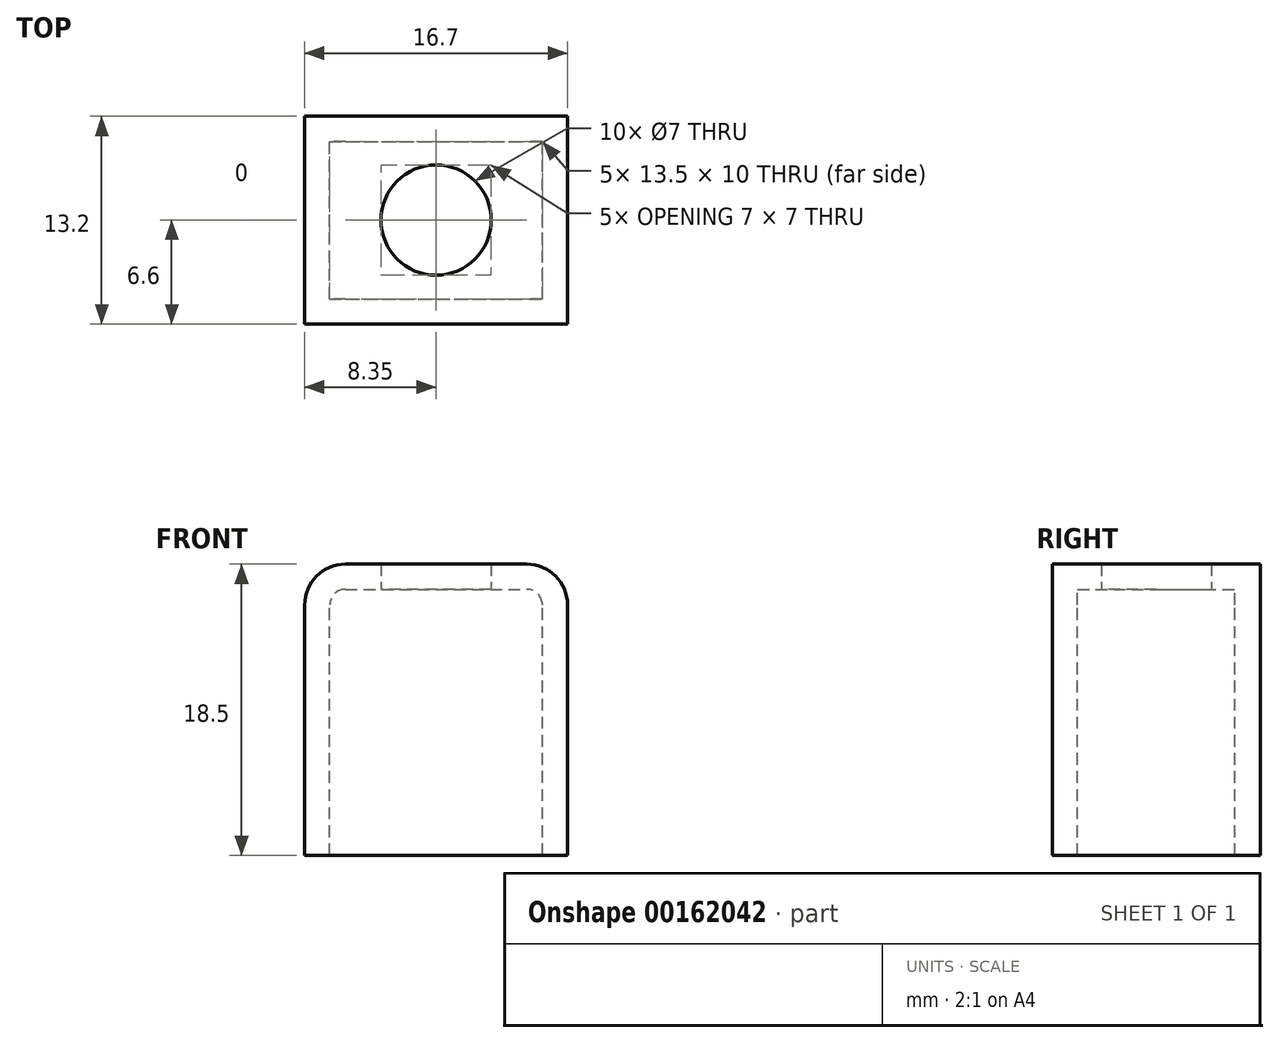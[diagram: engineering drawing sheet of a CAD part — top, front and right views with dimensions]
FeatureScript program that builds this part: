
annotation { "Feature Type Name" : "Feature", "Feature Type Description" : "" }
export const myFeature = defineFeature(function(context is Context, id is Id, definition is map)
    precondition{}
    {
        {
            var Q0;
            Q0=qCreatedBy(makeId("Front.planeOp"),FACE);
            var sketch = newSketch(context, id + "F0", { "sketchPlane" : qUnion([Q0])});
            skLineSegment(sketch, "E0.bottom", {"start": v(-8.35, 0) * mm, "end": v(8.35, 0) * mm});
            skLineSegment(sketch, "E0.top", {"start": v(-5.76, 18.5) * mm, "end": v(5.76, 18.5) * mm});
            skLineSegment(sketch, "E0.left", {"start": v(-8.35, 0) * mm, "end": v(-8.35, 15.9) * mm});
            skLineSegment(sketch, "E0.right", {"start": v(8.35, 0) * mm, "end": v(8.35, 15.9) * mm});
            skPoint(sketch, "E1.visualSharp", {"position": v(-8.35, 18.5) * mm});
            skArc(sketch, "E1.filletArc", {"start": v(-5.76, 18.5) * mm, "mid": v(-7.59, 17.74) * mm, "end": v(-8.35, 15.9) * mm});
            skPoint(sketch, "E2.visualSharp", {"position": v(8.35, 18.5) * mm});
            skArc(sketch, "E2.filletArc", {"start": v(8.35, 15.9) * mm, "mid": v(7.59, 17.74) * mm, "end": v(5.76, 18.5) * mm});
            skSolve(sketch);
        }
        {
            var Q0;
            Q0=qSketchRegion(id+"F0",true);
            extrude(context, id + "F1", {"entities" : qUnion([Q0]), "depth" : ((2 * 1.6) + 10) * mm});
        }
        {
            var Q0;
            Q0=makeQuery(id+"F1.opExtrude","SWEPT_FACE",FACE,{"disambiguationData":[OSD([sQuery(id+"F0.wireOp",EDGE,"E0.bottom")])]});
            shell(context, id + "F2", {"entities" : qUnion([Q0]), "thickness" : 1.6 * mm});
        }
        {
            var Q0;
            Q0=makeQuery(id+"F1.opExtrude","SWEPT_FACE",FACE,{"disambiguationData":[OSD([sQuery(id+"F0.wireOp",EDGE,"E0.top")])]});
            var sketch = newSketch(context, id + "F3", { "sketchPlane" : qUnion([Q0])});
            skPoint(sketch, "E3", {"position": v(0, -6.6) * mm});
            skCircle(sketch, "E4.cCircle", {"center": v(0, -6.6) * mm, "radius": 5.5 * mm, "construction": true});
            skLineSegment(sketch, "E4.0", {"start": v(0, -1.1) * mm, "end": v(4.76, -3.85) * mm, "construction": true});
            skLineSegment(sketch, "E4.1", {"start": v(4.76, -3.85) * mm, "end": v(4.76, -9.35) * mm, "construction": true});
            skLineSegment(sketch, "E4.2", {"start": v(4.76, -9.35) * mm, "end": v(0, -12.1) * mm, "construction": true});
            skLineSegment(sketch, "E4.3", {"start": v(0, -12.1) * mm, "end": v(-4.76, -9.35) * mm, "construction": true});
            skLineSegment(sketch, "E4.4", {"start": v(-4.76, -9.35) * mm, "end": v(-4.76, -3.85) * mm, "construction": true});
            skLineSegment(sketch, "E4.5", {"start": v(-4.76, -3.85) * mm, "end": v(0, -1.1) * mm, "construction": true});
            skSolve(sketch);
        }
        {
            var Q0;
            Q0=sQuery(id+"F3.wireOp",VERTEX,"E3");
            var Q1;
            Q1=makeQuery(id+"F1.opExtrude","SWEPT_BODY",BODY,{"disambiguationData":[OSD([sQuery(id+"F0.wireOp",EDGE,"E0.bottom"),sQuery(id+"F0.wireOp",EDGE,"E0.top"),sQuery(id+"F0.wireOp",EDGE,"E0.left"),sQuery(id+"F0.wireOp",EDGE,"E0.right"),sQuery(id+"F0.wireOp",EDGE,"E1.filletArc"),sQuery(id+"F0.wireOp",EDGE,"E2.filletArc")])]});
            hole(context, id + "F4", {"style" : HoleStyle.SIMPLE, "endStyle" : HoleEndStyle.THROUGH, "standardTappedOrClearance" : lookupTablePath({ "standard" : "ISO", "size" : "7", "type" : "Drilled" }), "standardBlindInLast" : lookupTablePath({ "standard" : "ISO", "size" : "7", "type" : "Drilled" }), "holeDiameter" : 7 * mm, "tappedDepth" : 12 * mm, "tapClearance" : 3, "startFromSketch" : true, "locations" : qUnion([Q0]), "scope" : qUnion([Q1])});
        }
    });
